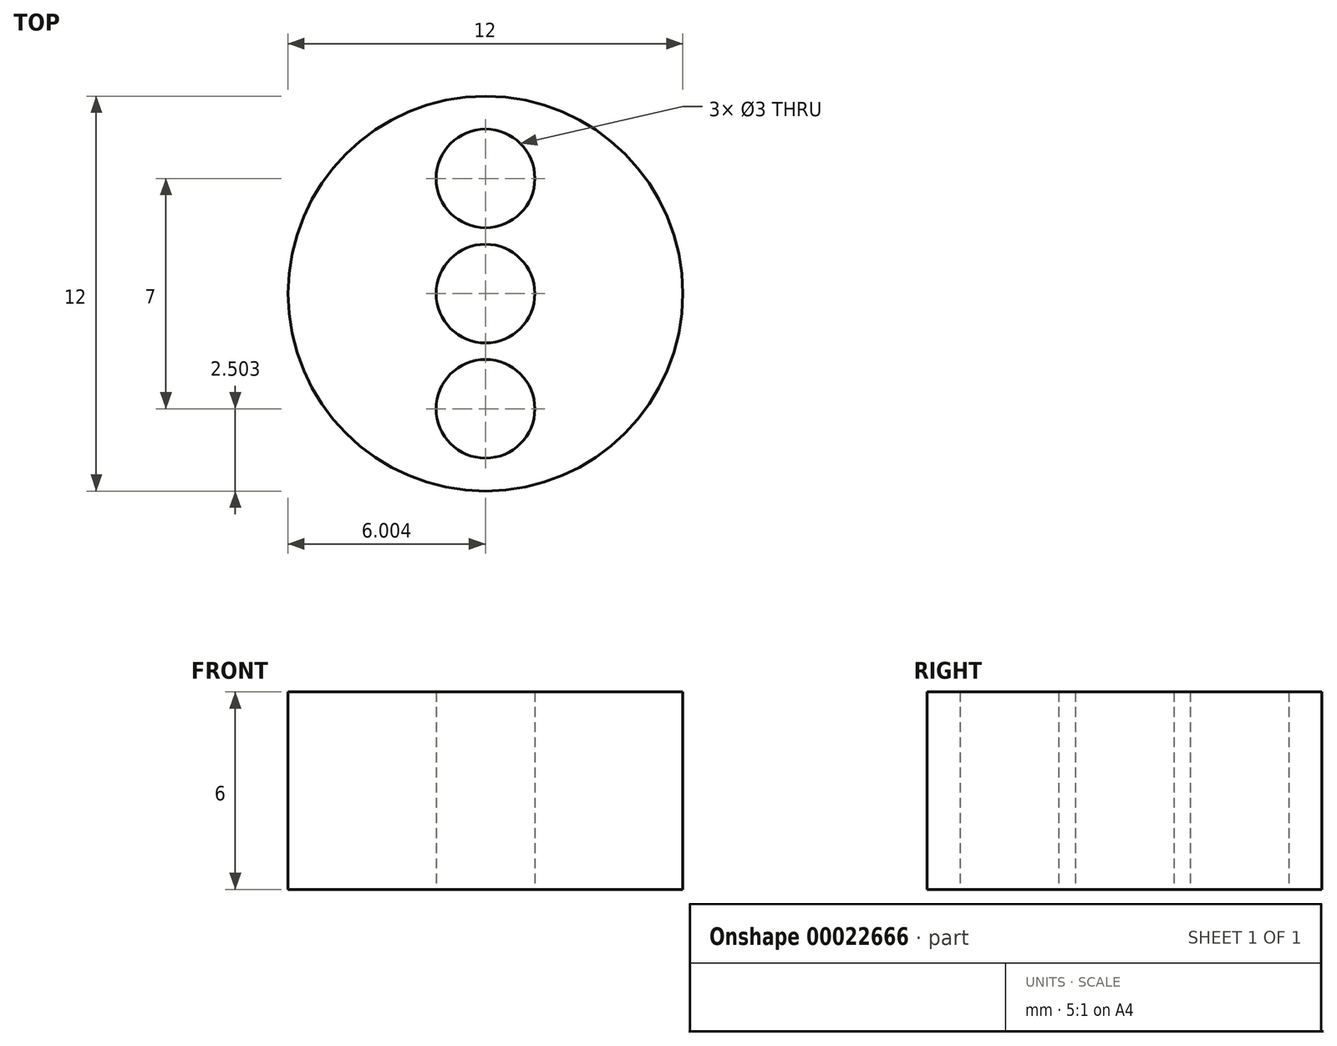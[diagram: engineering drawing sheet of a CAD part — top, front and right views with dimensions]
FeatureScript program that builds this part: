
annotation { "Feature Type Name" : "Feature", "Feature Type Description" : "" }
export const myFeature = defineFeature(function(context is Context, id is Id, definition is map)
    precondition{}
    {
        {
            var Q0;
            Q0=qCreatedBy(makeId("Top.planeOp"),FACE);
            var sketch = newSketch(context, id + "F0", { "sketchPlane" : qUnion([Q0])});
            skCircle(sketch, "E0", {"center": v(-34.32, 29.18) * mm, "radius": 6 * mm});
            skCircle(sketch, "E1", {"center": v(-34.32, 29.18) * mm, "radius": 1.5 * mm});
            skCircle(sketch, "E2", {"center": v(-34.32, 32.68) * mm, "radius": 1.5 * mm});
            skCircle(sketch, "E3.1.0", {"center": v(-34.32, 25.68) * mm, "radius": 1.5 * mm});
            skSolve(sketch);
        }
        {
            var Q0;
            Q0=makeQuery(id+"F0.imprint","IMPRINT",FACE,{"disambiguationData":[TD([[makeQuery(id+"F0.imprint","IMPRINT",EDGE,{"derivedFrom":sQuery(id+"F0.wireOp",EDGE,"E0")}),1.0]])]});
            extrude(context, id + "F1", {"entities" : qUnion([Q0]), "depth" : 6 * mm});
        }
    });
